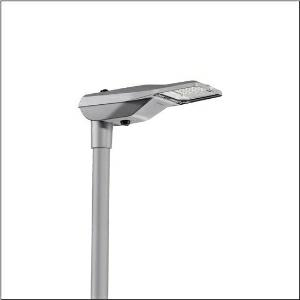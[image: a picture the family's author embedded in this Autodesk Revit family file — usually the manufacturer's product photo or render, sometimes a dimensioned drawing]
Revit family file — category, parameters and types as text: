
# Revit family: streetlight_sl_21_iq_micro___p0_8a_5xe1u31y08cb_2316
name_source: partatom
category: Lighting Fixtures
units: mm (PartAtom-declared; Revit-internal decimal feet)

## family parameters
Cut with Voids When Loaded = No
Host = Face
Light Source = No
Part Type = Normal
Room Calculation Point = No
Round Connector Dimension = Use Diameter
Shared = No

## types (1)
- --- (1 x LED, 2890 lm, 19.1 W, 3000K)
    Apparent Load = 19 VA
    CIE Flux Codes = 33 69 96 100 100
    Color Rendering = 70
    Color Temperature = 3000K
    Default Elevation = 1800 mm
    Description = Streetlight SL 21 iQ micro, mast luminaire, primary light control with lens, of PMMA, primary optical cover: cover, of toughened safety glass, transparent, light distribution: P0.8a, light emission: direct distribution, primary light characteristic: asymmetric, installation type: post-top, side-entry, LED, High Power LED, rated luminous flux: 2.890lm, luminous efficacy: 151lm/W, light colour: 730, colour temperature: 3000K, control gear: iQ-Street Remote, D4i with power reduction, control: pre-setting: logarithmic dimming characteristic, Street-Remote, Auto-Match, Temp-Guard, Lumen-Switch, Night-Set, Smart-Wire, Light-Fading, Desk-Remote (wireless, voltage-free reading and setting of iQ features in the workshop via application-optimized NFC function/RFID function), optimised constant luminous flux control (CLO 2.0), mains connection: 220..240V, AC, 50/60Hz, start of lifetime: 19W, end of service life: 20W, reduction: 9W, luminaire housing, of diecast aluminium, powder-coated, Siteco® metallic grey (DB 702S), corrosivity category C5 mid according to DIN EN ISO 12944, please order mast flange separately, inclination adjustable: 0°, 5°, 10°, 15°, sealing non-destructively replaceable, multi-level sealing system, length: 528mm, width: 235mm, height: 110mm, mast flange for spigot size: 42mm (side-entry): 5XC10008XM4, 60/48mm (side-entry/post-top): 5XC10108XM2, 76/60mm (side-entry/post-top): 5XC10108XM1, mounting height: 4..8m, Smart Interface below and above, protection rating (complete): IP66, insulation class (complete): insulation class II (safety insulation), certification: CE, ENEC, ENEC+, VDE, impact resistance: IK10, permissible operating ambient temperature for outdoor applications: -40..+50°C, standard-compliant lighting for roads and squares, packaging unit: 1 piece

Light Distribution: P0.8a
    Height = 110 mm
    Lamp = 1 x LED
    Lamp Light Flux = 2890 lm
    Lamp Power = 19.1 W
    Lamp count = 1
    Length = 528 mm
    Luminous efficacy = 151 lm/W
    Manufacturer = Siteco
    ModVariant = No
    Model = 5XE1U31Y08CB
    Number of Poles = 1
    OnlyDefault = Yes
    Power Factor = 1
    Product Name = Streetlight SL 21 iQ micro | P0.8a
    Product group = mast luminaire | pylon top
    ProductGroupID = 6100
    Protection Class = Protection class II
    Protection Degree = IP 66
    RLX_Detail_Level = 1
    RLX_Emergency_Light_Flux = 0 lm
    RLX_Emergency_Type = 0
    RLX_Emergency_Type_DB = No
    RlxData = <blob elided: 98245 chars, md5=2898dd85>
    Socket = socket
    Standby Power = 0 W
    System Light Flux = 2890 lm
    System Power = 19 W
    Type Comments = factory setting: luminous flux: 100 % | dim-lin: 254 | 387 mA
    Type Image = l_1007239.jpg
    URL = http://relux.com
    VarID = @adj_072890
    Voltage = 0 V
    Weight = 0.00 kg
    Width = 235 mm

## geometry (parser evidence)
native form markers: Blend x4, Sweep x11
no freeform markers — native parametric forms only
